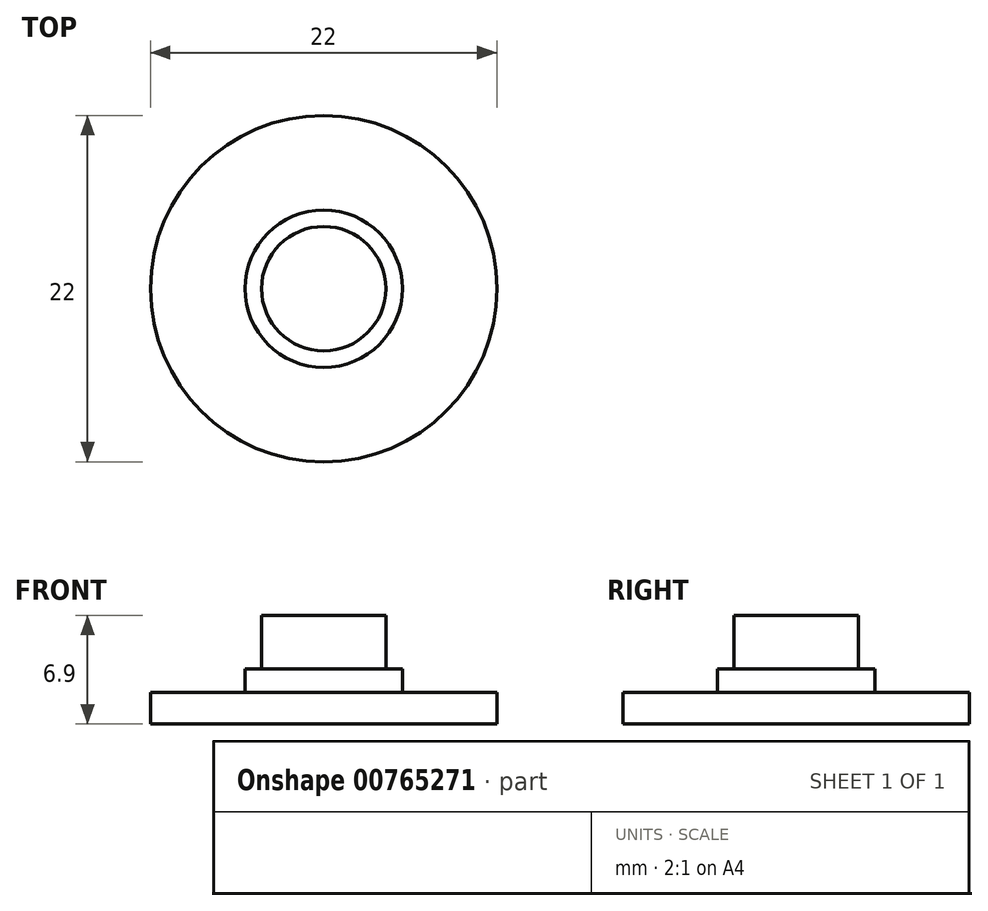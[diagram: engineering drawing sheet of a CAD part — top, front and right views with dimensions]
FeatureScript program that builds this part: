
annotation { "Feature Type Name" : "Feature", "Feature Type Description" : "" }
export const myFeature = defineFeature(function(context is Context, id is Id, definition is map)
    precondition{}
    {
        {
            var Q0;
            Q0=qCreatedBy(makeId("Top.planeOp"),FACE);
            var sketch = newSketch(context, id + "F0", { "sketchPlane" : qUnion([Q0])});
            skCircle(sketch, "E0", {"center": v(0, 0) * mm, "radius": 11 * mm});
            skCircle(sketch, "E1", {"center": v(0, 0) * mm, "radius": 5 * mm});
            skSolve(sketch);
        }
        {
            var Q0;
            Q0=makeQuery(id+"F0.imprint","IMPRINT",FACE,{"disambiguationData":[TD([[makeQuery(id+"F0.imprint","IMPRINT",EDGE,{"derivedFrom":sQuery(id+"F0.wireOp",EDGE,"E0")}),1.0]])]});
            var Q1;
            Q1=makeQuery(id+"F0.imprint","IMPRINT",FACE,{"disambiguationData":[TD([[makeQuery(id+"F0.imprint","IMPRINT",EDGE,{"derivedFrom":sQuery(id+"F0.wireOp",EDGE,"E1")}),1.0]])]});
            extrude(context, id + "F1", {"entities" : qUnion([Q0, Q1]), "oppositeDirection" : true, "depth" : 2 * mm, "offsetDistance" : 25 * mm});
        }
        {
            var Q0;
            Q0=makeQuery(id+"F0.imprint","IMPRINT",FACE,{"disambiguationData":[TD([[makeQuery(id+"F0.imprint","IMPRINT",EDGE,{"derivedFrom":sQuery(id+"F0.wireOp",EDGE,"E1")}),1.0]])]});
            extrude(context, id + "F2", {"entities" : qUnion([Q0]), "operationType" : NewBodyOperationType.ADD, "depth" : 1.5 * mm, "offsetDistance" : 25 * mm});
        }
        {
            var Q0;
            Q0=makeQuery(id+"F2.opExtrude","CAP_FACE",FACE,{"disambiguationData":[OSD([sQuery(id+"F0.wireOp",EDGE,"E1")])],"isStart":false});
            var sketch = newSketch(context, id + "F3", { "sketchPlane" : qUnion([Q0])});
            skCircle(sketch, "E2", {"center": v(0, 0) * mm, "radius": 3.95 * mm});
            skSolve(sketch);
        }
        {
            var Q0;
            Q0=qSketchRegion(id+"F3",true);
            extrude(context, id + "F4", {"entities" : qUnion([Q0]), "operationType" : NewBodyOperationType.ADD, "depth" : 3.4 * mm, "offsetDistance" : 25 * mm});
        }
    });
